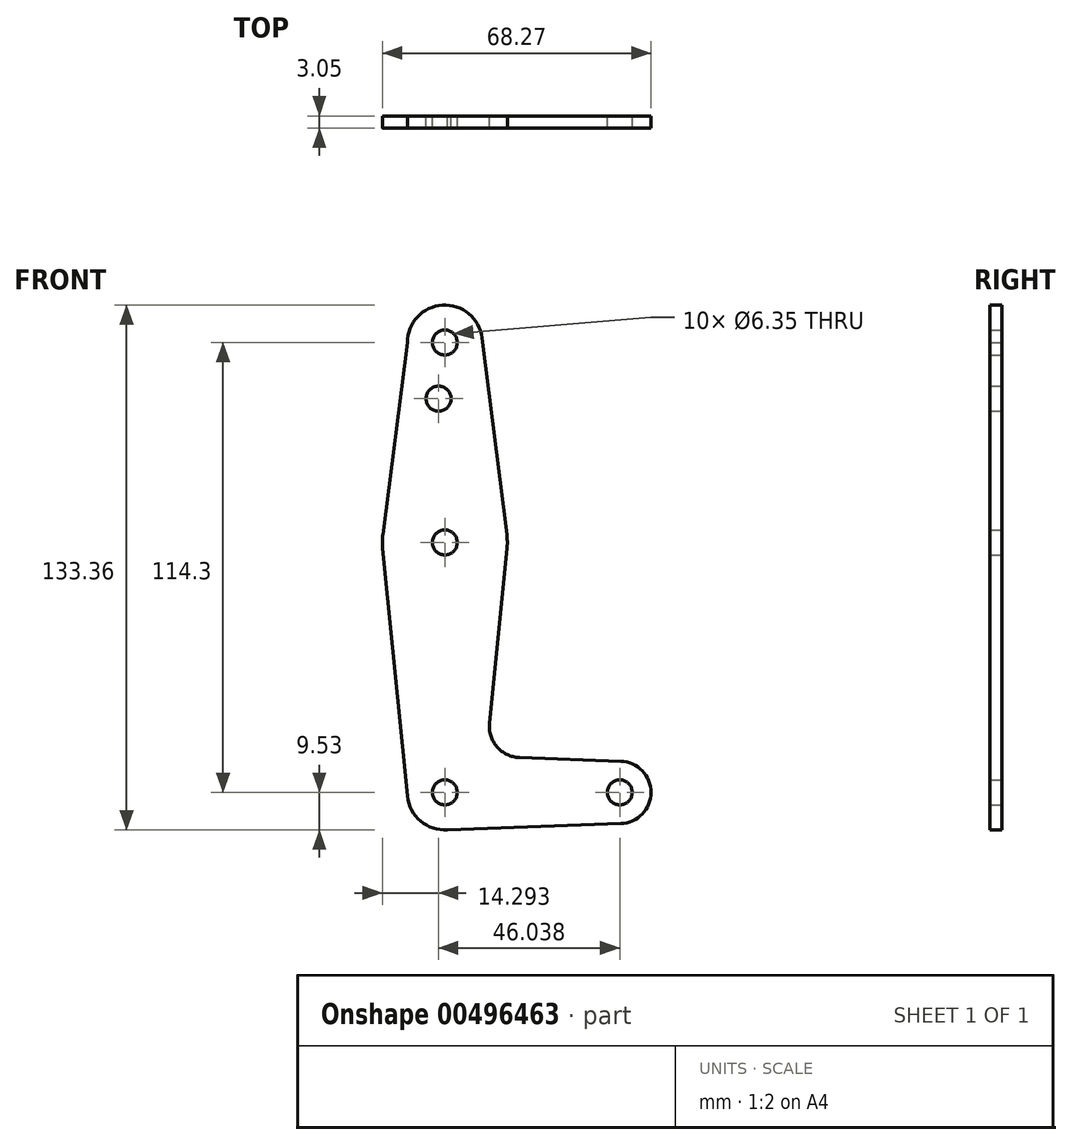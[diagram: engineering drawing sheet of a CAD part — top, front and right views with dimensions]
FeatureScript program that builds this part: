
annotation { "Feature Type Name" : "Feature", "Feature Type Description" : "" }
export const myFeature = defineFeature(function(context is Context, id is Id, definition is map)
    precondition{}
    {
        {
            var Q0;
            Q0=qCreatedBy(makeId("Front.planeOp"),FACE);
            var sketch = newSketch(context, id + "F0", { "sketchPlane" : qUnion([Q0])});
            skLineSegment(sketch, "E0", {"start": v(0, 114.3) * mm, "end": v(0, 0) * mm, "construction": true});
            skLineSegment(sketch, "E1", {"start": v(0, 0) * mm, "end": v(44.45, 0) * mm, "construction": true});
            skCircle(sketch, "E2", {"center": v(0, 114.3) * mm, "radius": 9.53 * mm});
            skCircle(sketch, "E3", {"center": v(0, 0) * mm, "radius": 9.53 * mm});
            skCircle(sketch, "E4", {"center": v(44.45, 0) * mm, "radius": 7.94 * mm});
            skCircle(sketch, "E5", {"center": v(0, 63.5) * mm, "radius": 15.88 * mm});
            skLineSegment(sketch, "E6", {"start": v(-9.52, 114.3) * mm, "end": v(-15.75, 65.5) * mm});
            skLineSegment(sketch, "E7", {"start": v(9.45, 115.5) * mm, "end": v(15.75, 65.48) * mm});
            skLineSegment(sketch, "E8", {"start": v(0, -9.53) * mm, "end": v(44.73, -7.93) * mm});
            skCircle(sketch, "E9", {"center": v(0, 63.5) * mm, "radius": 3.18 * mm});
            skCircle(sketch, "E10", {"center": v(44.45, 0) * mm, "radius": 3.18 * mm});
            skCircle(sketch, "E11", {"center": v(0, 0) * mm, "radius": 3.18 * mm});
            skCircle(sketch, "E12", {"center": v(0, 114.3) * mm, "radius": 3.18 * mm});
            skCircle(sketch, "E13", {"center": v(-1.59, 100.03) * mm, "radius": 3.18 * mm});
            skLineSegment(sketch, "E14", {"start": v(15.8, 61.91) * mm, "end": v(11.34, 17.6) * mm});
            skLineSegment(sketch, "E15", {"start": v(18.97, 8.85) * mm, "end": v(44.73, 7.93) * mm});
            skArc(sketch, "E16.filletArc", {"start": v(11.34, 17.6) * mm, "mid": v(13.26, 11.57) * mm, "end": v(18.97, 8.85) * mm});
            skLineSegment(sketch, "E17", {"start": v(-15.8, 61.91) * mm, "end": v(-9.48, -0.95) * mm});
            skSolve(sketch);
        }
        {
            var Q0;
            Q0 = qSketchRegion(id + "F0", true);
            extrude(context, id + "F1", {"entities" : qUnion([Q0]), "depth" : 3.05 * mm});
        }
        {
            var Q0;
            Q0 = qSketchRegion(id + "F0", true);
            extrude(context, id + "F2", {"entities" : qUnion([Q0]), "depth" : 3.05 * mm});
        }
    });
